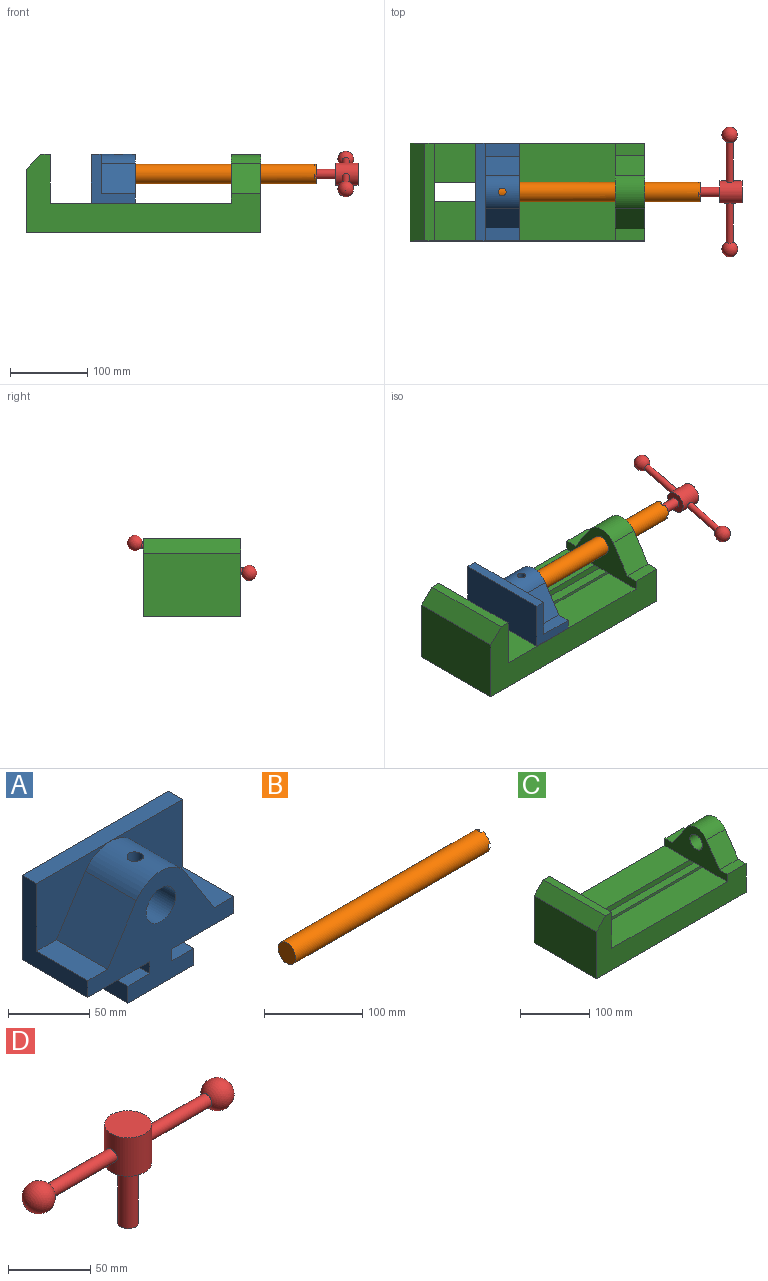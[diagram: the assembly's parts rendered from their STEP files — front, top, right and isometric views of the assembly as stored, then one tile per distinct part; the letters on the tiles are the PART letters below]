
ASSEMBLY  parts=4 mates=3
PART A: 24 faces, bbox 127x57.2x85.1 mm
  f0: plane 127x85.09mm, normal (0,-1,0), area 5003mm2, adj f3,f4,f5,f7,f8,f9,f10,f11
  f1: plane 127x12.7mm, normal (0,0,1), area 1612.9mm2, adj f3,f5,f6,f20,f23
  f2: cylinder r=5.08mm len=13.76mm, axis (0,0,1), area 413.9mm2, adj f15,f17
  f3: plane 63.5x57.15mm, normal (-1,0,0), area 1371mm2, adj f0,f1,f6,f11,f19,f20
  f4: plane 57.15x57.15mm, normal (0,0,-1), area 3266.1mm2, adj f0,f6,f10,f12
  f5: plane 63.5x57.15mm, normal (1,0,0), area 1371mm2, adj f0,f1,f6,f7,f21,f23
  f6: plane 127x85.09mm, normal (0,1,0), area 8959.7mm2, adj f1,f3,f4,f5,f7,f8,f9,f10
  f7: plane 57.15x53.98mm, normal (0,0,-1), area 3084.7mm2, adj f0,f5,f6,f8
  f8: plane 57.15x8.89mm, normal (1,0,0), area 508.1mm2, adj f0,f6,f7,f9
  f9: plane 57.15x19.05mm, normal (0,0,1), area 1088.7mm2, adj f0,f6,f8,f10
  f10: plane 57.15x12.7mm, normal (1,0,0), area 725.8mm2, adj f0,f4,f6,f9
  f11: plane 57.15x53.98mm, normal (0,0,-1), area 3084.7mm2, adj f0,f3,f6,f14
  f12: plane 57.15x12.7mm, normal (-1,0,0), area 725.8mm2, adj f0,f4,f6,f13
  f13: plane 57.15x19.05mm, normal (0,0,1), area 1088.7mm2, adj f0,f6,f12,f14
  f14: plane 57.15x8.89mm, normal (-1,0,0), area 508.1mm2, adj f0,f6,f11,f13
  f15: cylinder r=12.7mm len=44.45mm, axis (0,-1,0), area 3464.1mm2, adj f0,f2,f16
  f16: plane 25.4x25.4mm, normal (0,-1,0), area 506.7mm2, adj f15
  f17: cylinder r=25.4mm len=44.45mm, axis (0,-1,0), area 2182.3mm2, adj f0,f2,f18,f20,f22,f23
  f18: plane 44.45x39.07mm, normal (-0.84,0,0.54), area 2060.5mm2, adj f0,f17,f19,f20
  f19: plane 44.45x17.15mm, normal (0,0,1), area 762.1mm2, adj f0,f3,f18,f20
  f20: plane 63.5x50.8mm, normal (0,-1,0), area 1725mm2, adj f1,f3,f17,f18,f19
  f21: plane 44.45x17.15mm, normal (0,0,1), area 762.1mm2, adj f0,f5,f22,f23
  f22: plane 44.45x39.07mm, normal (0.84,0,0.54), area 2060.5mm2, adj f0,f17,f21,f23
  f23: plane 63.5x50.8mm, normal (0,-1,0), area 1725mm2, adj f1,f5,f17,f21,f22
PART B: 20 faces, bbox 279.4x25.4x25.4 mm
  f0: plane 9.9x9.9mm, normal (1,0,0), area 62.3mm2, adj f3,f6,f12,f17
  f1: plane 9.9x9.9mm, normal (1,0,0), area 62.3mm2, adj f3,f6,f14,f18
  f2: plane 9.9x9.9mm, normal (1,0,0), area 62.3mm2, adj f3,f6,f8,f11
  f3: cylinder r=12.7mm len=279.4mm, axis (-1,0,0), area 22243.2mm2, adj f0,f1,f2,f4,f5,f8,f9,f10
  f4: plane 9.9x9.9mm, normal (1,0,0), area 62.3mm2, adj f3,f6,f9,f15
  f5: plane 25.4x25.4mm, normal (-1,0,0), area 506.7mm2, adj f3
  f6: cylinder r=6.35mm len=19.05mm, axis (1,0,0), area 707mm2, adj f0,f1,f2,f4,f7,f8,f9,f10
  f7: plane 12.7x12.7mm, normal (1,0,0), area 126.7mm2, adj f6
  f8: plane 6.62x2.54mm, normal (0,-1,0), area 16.8mm2, adj f2,f3,f6,f10
  f9: plane 6.62x2.54mm, normal (0,1,0), area 16.8mm2, adj f3,f4,f6,f10
  f10: plane 6.88x5.08mm, normal (1,0,0), area 32.7mm2, adj f3,f6,f8,f9
  f11: plane 6.62x2.54mm, normal (0,0,1), area 16.8mm2, adj f2,f3,f6,f13
  f12: plane 6.62x2.54mm, normal (0,0,-1), area 16.8mm2, adj f0,f3,f6,f13
  f13: plane 6.88x5.08mm, normal (1,0,0), area 32.7mm2, adj f3,f6,f11,f12
  f14: plane 6.62x2.54mm, normal (0,0,-1), area 16.8mm2, adj f1,f3,f6,f16
  f15: plane 6.62x2.54mm, normal (0,0,1), area 16.8mm2, adj f3,f4,f6,f16
  f16: plane 6.88x5.08mm, normal (1,0,0), area 32.7mm2, adj f3,f6,f14,f15
  f17: plane 6.62x2.54mm, normal (0,-1,0), area 16.8mm2, adj f0,f3,f6,f19
  f18: plane 6.62x2.54mm, normal (0,1,0), area 16.8mm2, adj f1,f3,f6,f19
  f19: plane 6.88x5.08mm, normal (1,0,0), area 32.7mm2, adj f3,f6,f17,f18
PART C: 28 faces, bbox 304.8x127x101.6 mm
  f0: plane 234.95x50.8mm, normal (0,0,1), area 11935.5mm2, adj f1,f4,f8,f22
  f1: plane 127x63.5mm, normal (-1,0,0), area 4157.7mm2, adj f0,f3,f8,f9,f11,f12,f13,f14
  f2: plane 127x12.7mm, normal (0,0,1), area 1612.9mm2, adj f4,f8,f9,f10
  f3: plane 234.95x50.8mm, normal (0,0,1), area 11935.5mm2, adj f1,f4,f9,f21
  f4: plane 127x101.6mm, normal (1,0,0), area 9516.1mm2, adj f0,f2,f3,f6,f8,f9,f17,f18
  f5: plane 127x82.55mm, normal (-1,0,0), area 10483.8mm2, adj f6,f8,f9,f10
  f6: plane 304.8x127mm, normal (0,0,-1), area 31774.1mm2, adj f4,f5,f7,f8,f9,f17,f26
  f7: plane 127x101.6mm, normal (1,0,0), area 7544.8mm2, adj f6,f8,f9,f11,f12,f13,f14,f15
  f8: plane 304.8x101.6mm, normal (0,-1,0), area 13931.4mm2, adj f0,f1,f2,f4,f5,f6,f7,f10
  f9: plane 304.8x101.6mm, normal (0,1,0), area 13931.4mm2, adj f1,f2,f3,f4,f5,f6,f7,f10
  f10: plane 127x19.05mm, normal (-0.71,0,0.71), area 3421.5mm2, adj f2,f5,f8,f9
  f11: plane 39.55x38.1mm, normal (0,0.83,0.56), area 1814.5mm2, adj f1,f7,f12,f13
  f12: cylinder r=25.4mm len=42.19mm, axis (1,0,0), area 1896.6mm2, adj f1,f7,f11,f14
  f13: plane 38.1x15.88mm, normal (0,0,1), area 604.8mm2, adj f1,f7,f9,f11
  f14: plane 39.55x38.1mm, normal (0,-0.83,0.56), area 1814.5mm2, adj f1,f7,f12,f15
  f15: plane 38.1x15.88mm, normal (0,0,1), area 604.8mm2, adj f1,f7,f8,f14
  f16: plane 38.1x25.4mm, normal (0,0,-1), area 967.7mm2, adj f1,f7,f21,f22
  f17: plane 273.05x16.51mm, normal (0,-1,0), area 4508.1mm2, adj f4,f6,f7,f18
  f18: plane 273.05x19.05mm, normal (0,0,1), area 5201.6mm2, adj f4,f7,f17,f19
  f19: plane 273.05x12.7mm, normal (0,-1,0), area 3467.7mm2, adj f4,f7,f18,f20
  f20: plane 273.05x19.05mm, normal (0,0,-1), area 5201.6mm2, adj f4,f7,f19,f21
  f21: plane 273.05x8.89mm, normal (0,-1,0), area 2427.4mm2, adj f3,f4,f7,f16,f20
  f22: plane 273.05x8.89mm, normal (0,1,0), area 2427.4mm2, adj f0,f4,f7,f16,f23
  f23: plane 273.05x19.05mm, normal (0,0,-1), area 5201.6mm2, adj f4,f7,f22,f24
  f24: plane 273.05x12.7mm, normal (0,1,0), area 3467.7mm2, adj f4,f7,f23,f25
  f25: plane 273.05x19.05mm, normal (0,0,1), area 5201.6mm2, adj f4,f7,f24,f26
  f26: plane 273.05x16.51mm, normal (0,1,0), area 4508.1mm2, adj f4,f6,f7,f25
  f27: cylinder r=12.7mm len=38.1mm, axis (1,0,0), area 3040.2mm2, adj f1,f7
PART D: 9 faces, bbox 173.5x28.6x73 mm
  f0: cylinder r=4.45mm len=53.86mm, axis (-1,0,0), area 1494.4mm2, adj f1,f8
  f1: cylinder r=14.29mm len=28.58mm, axis (0,0,-1), area 2439.5mm2, adj f0,f2,f3,f6
  f2: plane 28.58x28.58mm, normal (0,0,1), area 641.3mm2, adj f1
  f3: plane 28.58x28.58mm, normal (0,0,-1), area 514.6mm2, adj f1,f4
  f4: cylinder r=6.35mm len=44.45mm, axis (0,0,1), area 1773.5mm2, adj f3,f5
  f5: plane 12.7x12.7mm, normal (0,0,-1), area 126.7mm2, adj f4
  f6: cylinder r=4.45mm len=53.86mm, axis (-1,0,0), area 1494.4mm2, adj f1,f7
  f7: sphere r=10.16mm, area 1231.8mm2, adj f6
  f8: sphere r=10.16mm, area 1231.8mm2, adj f0
PLACE A rot(axis=(0,0,1),90deg) t=(91.41,31.55,-4.63)mm
PLACE B rot(axis=(1,0,0),104.7deg) t=(75.54,95.05,55.06)mm
PLACE C t=(-22.02,95.05,-21.14)mm fixed
PLACE D rot(axis=(0.62,0.48,0.62),128.8deg) t=(394.62,95.05,55.06)mm
MATE fastened B.f3 <-> D.f1  axis (1,0,0) through (335.89,95.05,55.06)mm
MATE revolute A.f15 <-> B.f3  axis (1,0,0) through (75.54,95.05,55.06)mm
MATE slider C.f4 <-> A.f6  axis (-1,0,0) through (9.73,31.55,16.96)mm
